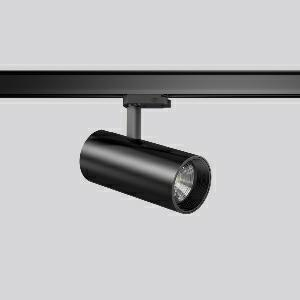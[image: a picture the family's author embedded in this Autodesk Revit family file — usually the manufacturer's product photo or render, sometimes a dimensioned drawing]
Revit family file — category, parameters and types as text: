
# Revit family: deecos_s_mini_742200_003_2_76_0698
name_source: partatom
category: Lighting Fixtures
units: mm (PartAtom-declared; Revit-internal decimal feet)

## family parameters
Cut with Voids When Loaded = No
Host = Face
Light Source = No
Part Type = Normal
Room Calculation Point = No
Round Connector Dimension = Use Diameter
Shared = No

## types (1)
- DEECOS S mini (1 x LED Modul 927, 1900 lm, 2700)
    Apparent Load = 20 VA
    Approval mark = CE
    CIE Flux Codes = 98 100 100 100 100
    Color Rendering = 92
    Color Temperature = 2700
    Default Elevation = 1800 mm
    Description = Series: DEECOS S mini
LED surface-mounted projector in modern design with no visible cooling ribs. Housing: die-cast aluminium, powder-coated. Rotation range: 356°. Swivel range: 90°. Black plastic ring and recessed LED to prevent glare from the side. Optical assembly with lens made of plastic (polycarbonate) for the best homogeneous light distribution - can be changed without tools. Best colour rendering index Ra>90. With adapter for RZB 3-circuit DALI tracks. Suitable for Track on ceiling, Wall track. High quality converter without flickering and stroboscopic effect. The following accessories can be mounted without use of tools: interchangeable lenses, decorative glasses, honeycomb louvre, clear and frosted diffusers, white interchangeable plastic ring. 
Colour: deep black, matt (RAL 9005)
Diameter: 87 mm
Height: 214 mm
Lamp: LED
Socket: without socket
Colour temperature: 2700K
Colour rendering index (CRI): 92
System power: 20 W
Rated luminous flux: 1900 lm
Luminous efficiency: 95 lm/W
Control gear: Converter, dimmable, DALI
Protection class: I
Type of protection: IP 20
    Height = 214 mm
    Lamp = 1 x LED Modul 927
    Lamp Light Flux = 1900 lm
    Lamp count = 1
    Length = 87 mm
    Lifetime = 50000 h
    Luminous efficacy = 95 lm/W
    Manufacturer = RZB
    ModVariant = No
    Model = 742200.003.2.76
    Mounting Place = Ceiling
    Mounting Type = Rail mounted
    Number of Poles = 1
    OnlyDefault = Yes
    Power Factor = 1
    Product Name = DEECOS S mini
    Product group = Track mounted projectors
    ProductGroupID = 301
    Protection Class = Protection class I
    Protection Degree = IP 20
    RLX_Detail_Level = 1
    RLX_Emergency_Light_Flux = 0 lm
    RLX_Emergency_Type = 0
    RLX_Emergency_Type_DB = No
    RlxData = <blob elided: 38821 chars, md5=6f720199>
    Socket = socket
    Standby Power = 0 W
    System Light Flux = 1900 lm
    System Power = 20 W
    Type Comments = Product without accessories
    Type Image = 741930.003.jpg
    URL = http://relux.com
    VarID = ---
    Voltage = 230 V
    Voltage Range = 220-240 V
    Weight = 0.00 kg
    Width = 0 mm  [stored 0 ft]

note: [stored X ft] marks values corroborated as IEEE doubles in the binary element streams (Revit-internal decimal feet)

## geometry (parser evidence)
native form markers: Blend x4, Sweep x13
no freeform markers — native parametric forms only
